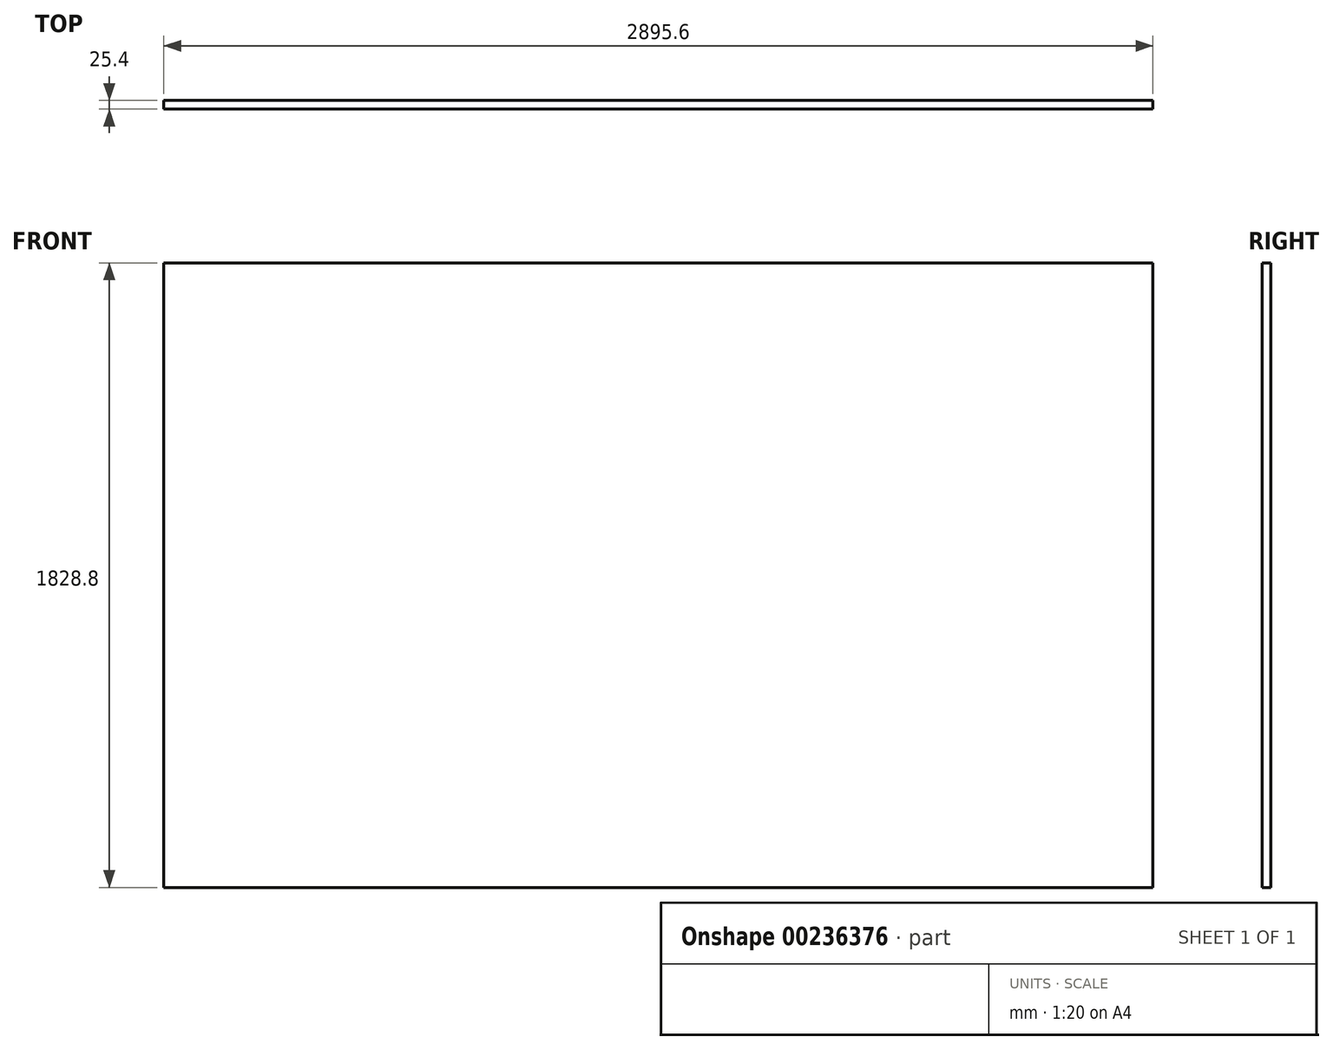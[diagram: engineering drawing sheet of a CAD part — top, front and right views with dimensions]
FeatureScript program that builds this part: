
annotation { "Feature Type Name" : "Feature", "Feature Type Description" : "" }
export const myFeature = defineFeature(function(context is Context, id is Id, definition is map)
    precondition{}
    {
        {
            var Q0;
            Q0=qCreatedBy(makeId("Front.planeOp"),FACE);
            var sketch = newSketch(context, id + "F0", { "sketchPlane" : qUnion([Q0])});
            skLineSegment(sketch, "E0.bottom", {"start": v(-1368.62, -18.4) * mm, "end": v(1526.98, -18.4) * mm});
            skLineSegment(sketch, "E0.top", {"start": v(-1368.62, -1847.2) * mm, "end": v(1526.98, -1847.2) * mm});
            skLineSegment(sketch, "E0.left", {"start": v(-1368.62, -18.4) * mm, "end": v(-1368.62, -1847.2) * mm});
            skLineSegment(sketch, "E0.right", {"start": v(1526.98, -18.4) * mm, "end": v(1526.98, -1847.2) * mm});
            skSolve(sketch);
        }
        {
            var Q0;
            Q0 = qSketchRegion(id + "F0", true);
            extrude(context, id + "F1", {"entities" : qUnion([Q0]), "depth" : 25.4 * mm});
        }
    });
